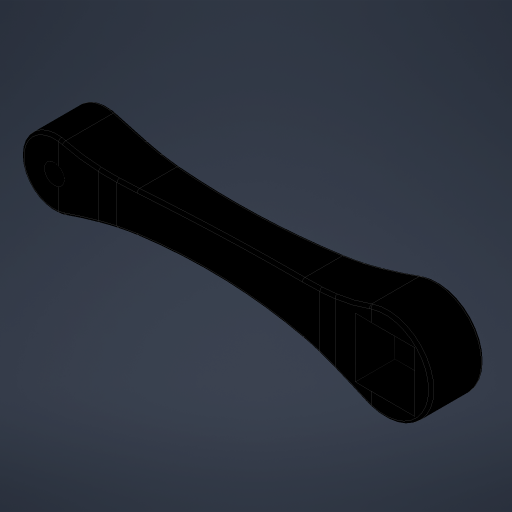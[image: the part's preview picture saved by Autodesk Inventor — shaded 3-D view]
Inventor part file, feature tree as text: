
AUTODESK INVENTOR PART (.ipt)
format: ipt  version: 2023 (Build 270158000, 158)  size: 477,696 bytes
history: native  units: mm
features: extrude x6, sketch x6, fillet x5, chamfer x4
ambient origin geometry x8: Origin, YZ Plane, XZ Plane, XY Plane, X Axis, Y Axis, Z Axis, Center Point
bodies: Solid1 (feature_tree)
feature tree (21):
  extrude  "Extrusion1"  Depth=250.0mm
  extrude  "Extrusion2"  TaperAngle=45.0deg  [1 undecoded]
  extrude  "Extrusion3"  Depth=40.0mm TaperAngle=0.0deg
  chamfer  "Chamfer1"  Distance=10.0mm
  chamfer  "Chamfer2"  Distance=10.0mm
  chamfer  "Chamfer3"  Distance=10.0mm Angle=45.0deg
  chamfer  "Chamfer4"  Distance=10.0mm Angle=45.0deg
  fillet  "Fillet1"  Radius=800.0mm
  extrude  "Extrusion4"  Depth=15.0mm
  fillet  "Fillet2"  Radius=40.0mm
  fillet  "Fillet3"  Radius=300.0mm
  extrude  "Extrusion5"  Depth=200.0mm
  extrude  "Extrusion7"  Depth=22.5mm
  fillet  "Fillet5"  Radius=22.5mm
  fillet  "Fillet6"  Radius=45.0mm
  sketch  "Sketch1"  dims[d0=50.0mm d1=250.0mm]
  sketch  "Sketch2"  dims[d2=70.0mm d3=45.0deg]
  sketch  "Sketch3"  dims[d4=135.0deg d5=40.0mm d6=0.0mm d7=10.0mm d8=0.0mm]
  sketch  "Sketch4"  dims[d9=49.497mm d10=10.0mm d11=0.0mm d12=10.0mm d13=103.787mm d14=45.0deg d15=10.0mm d16=103.786mm d17=45.0deg]
  sketch  "Sketch5"  dims[d18=10.0mm d19=103.786mm d20=45.0deg]
  sketch  "Sketch7"  dims[d21=10.0mm d22=103.787mm d23=45.0deg d24=800.0mm d25=15.0mm d26=40.0mm d27=0.0mm d28=300.0mm d29=200.0mm d30=22.5mm d31=22.5mm d32=45.0mm d33=45.0mm d34=30.0mm d35=0.0mm d40=50.0mm d41=5.0mm d42=0.0mm d43=2.0mm d44=2.0mm]
note: 1 required parameter value undecoded (feature->parameter linkage not recoverable at this tier; creation-order binding heuristic only, values carry confidence <= 0.55)
